# Revit family: P900014-031
name_source: partatom
category: Lighting Fixtures
revit_build: Autodesk Revit 2014 (Build: 20130308_1515(x64)
units: mm (PartAtom-declared; Revit-internal decimal feet)

## types (1)
- P900014-031
    Apparent Load = 60 VA
    Assembly Code = D5020200
    Connector Description = Lighting Connector
    Default Elevation = 48 "
    Description = Incorporate a hint of stylish industrial light to any commercial or residential setting with this brushed nickel four-head track metal directional light fixture. Multi-directional lamp heads provide design flexibility and illuminate typically hard-to-reach areas such as highlighting images in a lobby or gallery. The directional frame is coated in a beautiful black finish. Each lamp features an industrial styled-shade with an outer ribbed design and the capability to create different beam shapes as needed
    Features = Each lamp features an industrial styled-shade with an outer ribbed design and the capability to create different beam shapes as needed.
The directional frame is coated in a beautiful black finish.
Multi-directional lamp heads provide design flexibility and illuminate typically hard-to-reach areas
Ideal for any lobby, gallery, sitting room, hallway, or foyer.
Perfect for transitional or modern settings.
Measures 5-inch width by 6-7/16-inch height.
Uses four GU10 base bulbs that are sold separately (50w max - LED or incandescent).
Able to be fully dimmable with dimmable bulbs.
Includes installation instructions and mounting hardware.
Progress Lighting products are designed for exceptional quality, reliability, and functionality.
    Fixture distribution = Direct
    Glass = Paint - Hubbell - White Texture
    Gold = Hubbell - Gold
    Height = 26.5 "
    Housing Material = Paint - Hubbell - Textured Camera Black
    Lamp = LED or Medium Base
    Load Classification = Lighting
    Manufacturer = Progress Lighting
    Model = P900014-031
    Power Factor = 1
    Product Documentation Link = https://hubbellcdn.com
    Product Link = https://www.hubbell.com
    URL = https://www.hubbell.com
    Voltage = 120 V
    Warranty = 1 year Warranty
    Wattage Comments = 60W
    Watts = 60 W
    Width = 6 "

## geometry (parser evidence)
native form markers: Sweep x3
no freeform markers — native parametric forms only
